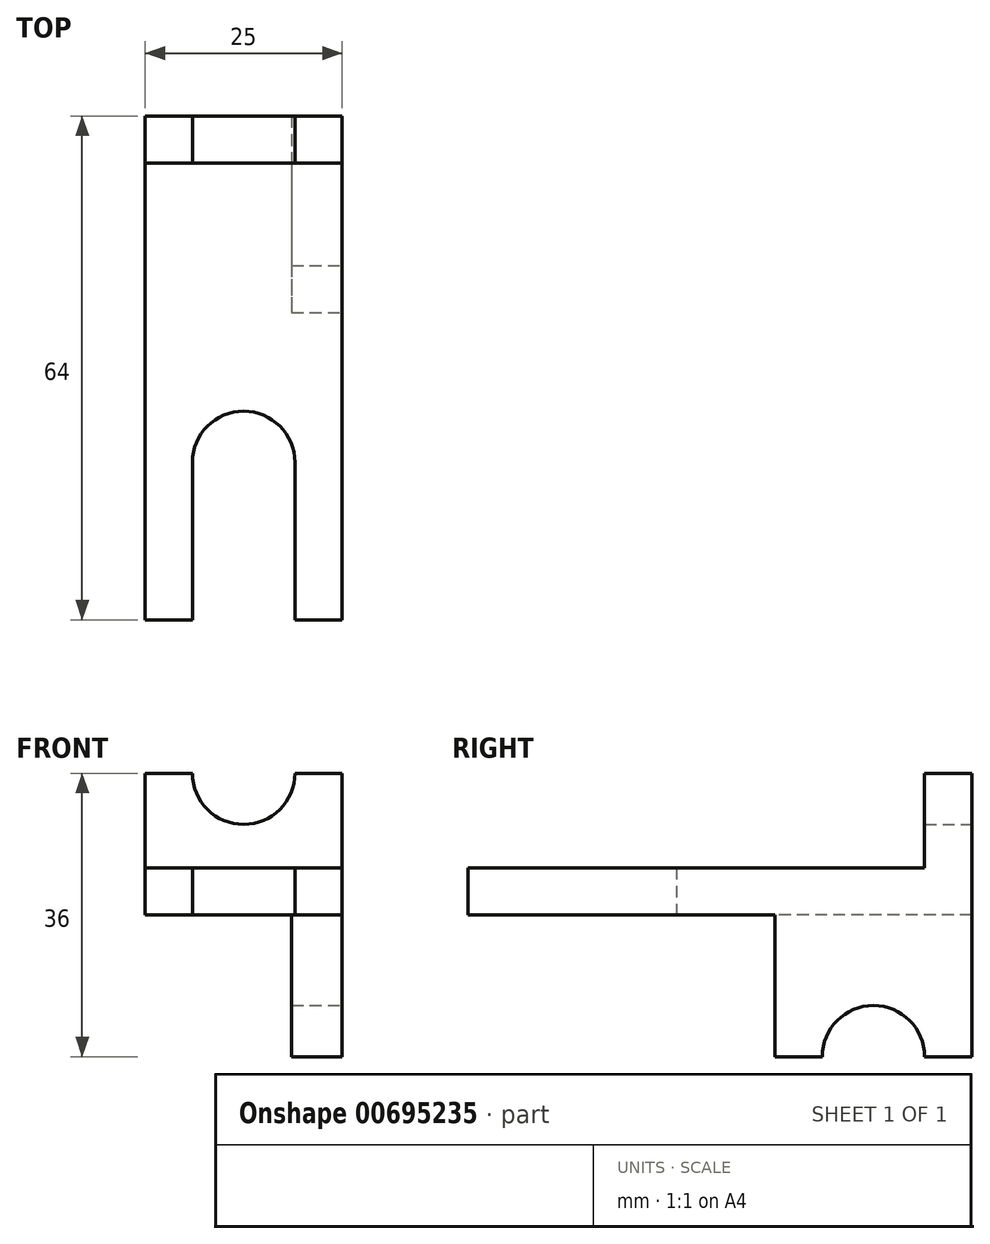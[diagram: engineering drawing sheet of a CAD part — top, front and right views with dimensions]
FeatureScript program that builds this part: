
annotation { "Feature Type Name" : "Feature", "Feature Type Description" : "" }
export const myFeature = defineFeature(function(context is Context, id is Id, definition is map)
    precondition{}
    {
        {
            var Q0;
            Q0=qCreatedBy(makeId("Top.planeOp"),FACE);
            var sketch = newSketch(context, id + "F0", { "sketchPlane" : qUnion([Q0])});
            skLineSegment(sketch, "E0.bottom", {"start": v(12.5, 32) * mm, "end": v(-12.5, 32) * mm});
            skLineSegment(sketch, "E0.top", {"start": v(12.5, -32) * mm, "end": v(-12.5, -32) * mm});
            skLineSegment(sketch, "E0.left", {"start": v(12.5, 32) * mm, "end": v(12.5, -32) * mm});
            skLineSegment(sketch, "E0.right", {"start": v(-12.5, 32) * mm, "end": v(-12.5, -32) * mm});
            skPoint(sketch, "E0.middle", {"position": v(0, 0) * mm});
            skPoint(sketch, "E1.middle", {"position": v(0, -32) * mm});
            skLineSegment(sketch, "E2.bottom", {"start": v(-6.5, -32) * mm, "end": v(6.5, -32) * mm});
            skLineSegment(sketch, "E2.top", {"start": v(-6.5, -12) * mm, "end": v(6.5, -12) * mm});
            skLineSegment(sketch, "E2.left", {"start": v(-6.5, -32) * mm, "end": v(-6.5, -12) * mm});
            skLineSegment(sketch, "E2.right", {"start": v(6.5, -32) * mm, "end": v(6.5, -12) * mm});
            skArc(sketch, "E3", {"start": v(-6.5, -12) * mm, "mid": v(0, -5.5) * mm, "end": v(6.5, -12) * mm});
            skSolve(sketch);
        }
        {
            var Q0;
            Q0=makeQuery(id+"F0.imprint","IMPRINT",FACE,{"disambiguationData":[TD([[makeQuery(id+"F0.imprint","IMPRINT",EDGE,{"derivedFrom":sQuery(id+"F0.wireOp",EDGE,"E0.bottom")}),1.0]])]});
            extrude(context, id + "F1", {"entities" : qUnion([Q0]), "depth" : 6 * mm, "offsetDistance" : 25 * mm});
        }
        {
            var Q0;
            Q0=makeQuery(id+"F1.opExtrude","SWEPT_FACE",FACE,{"disambiguationData":[OSD([sQuery(id+"F0.wireOp",EDGE,"E0.bottom")])]});
            var sketch = newSketch(context, id + "F2", { "sketchPlane" : qUnion([Q0])});
            skLineSegment(sketch, "E4.bottom", {"start": v(-12.5, 0) * mm, "end": v(12.5, 0) * mm});
            skLineSegment(sketch, "E4.top", {"start": v(-12.5, 18) * mm, "end": v(12.5, 18) * mm});
            skLineSegment(sketch, "E4.left", {"start": v(-12.5, 0) * mm, "end": v(-12.5, 18) * mm});
            skLineSegment(sketch, "E4.right", {"start": v(12.5, 0) * mm, "end": v(12.5, 18) * mm});
            skArc(sketch, "E5", {"start": v(-12.5, 18) * mm, "mid": v(0, 30.5) * mm, "end": v(12.5, 18) * mm});
            skCircle(sketch, "E6", {"center": v(0, 18) * mm, "radius": 6.5 * mm});
            skSolve(sketch);
        }
        {
            var Q0;
            {var subQ1=makeQuery(id+"F1.opExtrude","CAP_EDGE",EDGE,{"disambiguationData":[OSD([sQuery(id+"F0.wireOp",EDGE,"E0.bottom")])],"isStart":false});Q0=makeQuery(id+"F2.imprint","IMPRINT",FACE,{"disambiguationData":[TD([[makeQuery(id+"F2.imprint","IMPRINT",EDGE,{"derivedFrom":subQ1}),1.0]])]});}
            var Q1;
            {var subQ0=sQuery(id+"F2.wireOp",EDGE,"E5");Q1=makeQuery(id+"F2.imprint","IMPRINT",FACE,{"disambiguationData":[TD([[makeQuery(id+"F2.imprint","IMPRINT",EDGE,{"derivedFrom":subQ0}),-1.0]])]});}
            extrude(context, id + "F3", {"entities" : qUnion([Q0, Q1]), "operationType" : NewBodyOperationType.ADD, "oppositeDirection" : true, "depth" : 6 * mm, "offsetDistance" : 25 * mm});
        }
        {
            var Q0;
            Q0=makeQuery(id+"F3.boolean.opBoolean","MERGE",FACE,{"derivedFrom":[makeQuery(id+"F1.opExtrude","SWEPT_FACE",FACE,{"disambiguationData":[OSD([sQuery(id+"F0.wireOp",EDGE,"E0.left")])]}),makeQuery(id+"F3.opExtrude","SWEPT_FACE",FACE,{"disambiguationData":[OSD([sQuery(id+"F2.wireOp",EDGE,"E4.left")])]})]});
            var sketch = newSketch(context, id + "F4", { "sketchPlane" : qUnion([Q0])});
            skLineSegment(sketch, "E7.bottom", {"start": v(32, 0) * mm, "end": v(7, 0) * mm});
            skLineSegment(sketch, "E7.top", {"start": v(32, -18) * mm, "end": v(7, -18) * mm});
            skLineSegment(sketch, "E7.left", {"start": v(32, 0) * mm, "end": v(32, -18) * mm});
            skLineSegment(sketch, "E7.right", {"start": v(7, 0) * mm, "end": v(7, -18) * mm});
            skArc(sketch, "E8", {"start": v(32, -18) * mm, "mid": v(19.5, -30.5) * mm, "end": v(7, -18) * mm});
            skCircle(sketch, "E9", {"center": v(19.5, -18) * mm, "radius": 6.5 * mm});
            skSolve(sketch);
        }
        {
            var Q0;
            Q0=makeQuery(id+"F4.imprint","IMPRINT",FACE,{"disambiguationData":[TD([[makeQuery(id+"F4.imprint","IMPRINT",EDGE,{"derivedFrom":sQuery(id+"F4.wireOp",EDGE,"E7.bottom")}),1.0]])]});
            var Q1;
            {var subQ0=sQuery(id+"F4.wireOp",EDGE,"E8");Q1=makeQuery(id+"F4.imprint","IMPRINT",FACE,{"disambiguationData":[TD([[makeQuery(id+"F4.imprint","IMPRINT",EDGE,{"derivedFrom":subQ0}),-1.0]])]});}
            extrude(context, id + "F5", {"entities" : qUnion([Q0, Q1]), "operationType" : NewBodyOperationType.ADD, "oppositeDirection" : true, "depth" : 6.4 * mm, "offsetDistance" : 25 * mm});
        }
    });
